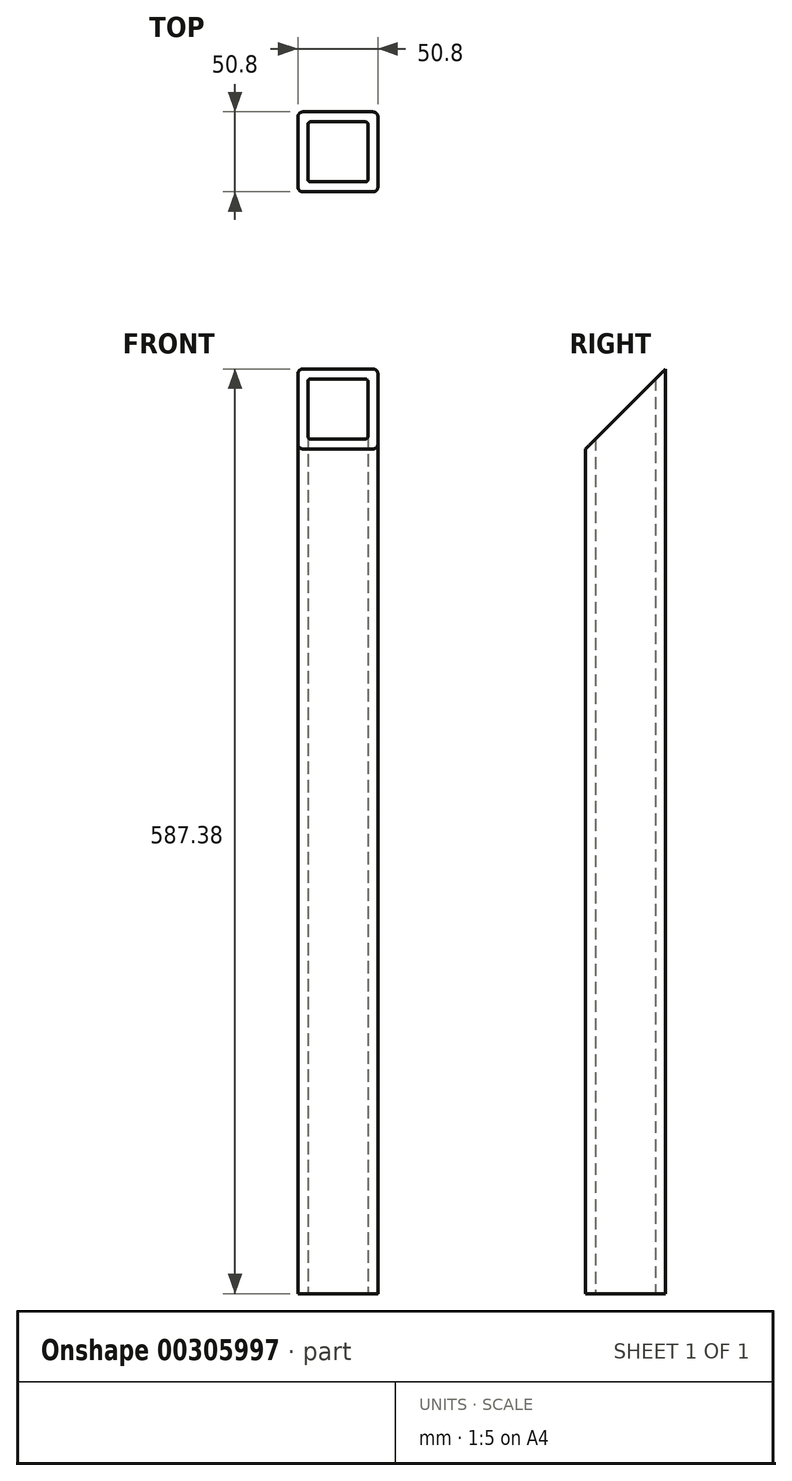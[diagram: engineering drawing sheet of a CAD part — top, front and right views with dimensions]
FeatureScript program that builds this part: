
annotation { "Feature Type Name" : "Feature", "Feature Type Description" : "" }
export const myFeature = defineFeature(function(context is Context, id is Id, definition is map)
    precondition{}
    {
        {
            var Q0;
            Q0=qCreatedBy(makeId("Top.planeOp"),FACE);
            var sketch = newSketch(context, id + "F0", { "sketchPlane" : qUnion([Q0])});
            skLineSegment(sketch, "E0.bottom", {"start": v(-22.22, 25.4) * mm, "end": v(22.23, 25.4) * mm});
            skLineSegment(sketch, "E0.top", {"start": v(-22.23, -25.4) * mm, "end": v(22.23, -25.4) * mm});
            skLineSegment(sketch, "E0.left", {"start": v(-25.4, 22.22) * mm, "end": v(-25.4, -22.23) * mm});
            skLineSegment(sketch, "E0.right", {"start": v(25.4, 22.22) * mm, "end": v(25.4, -22.23) * mm});
            skPoint(sketch, "E0.middle", {"position": v(0, 0) * mm});
            skPoint(sketch, "E1.visualSharp", {"position": v(-25.4, 25.4) * mm});
            skArc(sketch, "E1.filletArc", {"start": v(-22.22, 25.4) * mm, "mid": v(-24.47, 24.47) * mm, "end": v(-25.4, 22.22) * mm});
            skPoint(sketch, "E2.visualSharp", {"position": v(-25.4, -25.4) * mm});
            skArc(sketch, "E2.filletArc", {"start": v(-25.4, -22.23) * mm, "mid": v(-24.47, -24.47) * mm, "end": v(-22.23, -25.4) * mm});
            skPoint(sketch, "E3.visualSharp", {"position": v(25.4, -25.4) * mm});
            skArc(sketch, "E3.filletArc", {"start": v(22.23, -25.4) * mm, "mid": v(24.47, -24.47) * mm, "end": v(25.4, -22.23) * mm});
            skPoint(sketch, "E4.visualSharp", {"position": v(25.4, 25.4) * mm});
            skArc(sketch, "E4.filletArc", {"start": v(25.4, 22.22) * mm, "mid": v(24.47, 24.47) * mm, "end": v(22.23, 25.4) * mm});
            skLineSegment(sketch, "E5.0", {"start": v(-17.46, 19.05) * mm, "end": v(17.46, 19.05) * mm});
            skLineSegment(sketch, "E5.1", {"start": v(-19.05, 17.46) * mm, "end": v(-19.05, -17.46) * mm});
            skLineSegment(sketch, "E5.2", {"start": v(-17.46, -19.05) * mm, "end": v(17.46, -19.05) * mm});
            skLineSegment(sketch, "E5.3", {"start": v(19.05, 17.46) * mm, "end": v(19.05, -17.46) * mm});
            skPoint(sketch, "E6.visualSharp", {"position": v(-19.05, 19.05) * mm});
            skArc(sketch, "E6.filletArc", {"start": v(-17.46, 19.05) * mm, "mid": v(-18.59, 18.59) * mm, "end": v(-19.05, 17.46) * mm});
            skPoint(sketch, "E7.visualSharp", {"position": v(-19.05, -19.05) * mm});
            skArc(sketch, "E7.filletArc", {"start": v(-19.05, -17.46) * mm, "mid": v(-18.59, -18.59) * mm, "end": v(-17.46, -19.05) * mm});
            skPoint(sketch, "E8.visualSharp", {"position": v(19.05, -19.05) * mm});
            skArc(sketch, "E8.filletArc", {"start": v(17.46, -19.05) * mm, "mid": v(18.59, -18.59) * mm, "end": v(19.05, -17.46) * mm});
            skPoint(sketch, "E9.visualSharp", {"position": v(19.05, 19.05) * mm});
            skArc(sketch, "E9.filletArc", {"start": v(19.05, 17.46) * mm, "mid": v(18.59, 18.59) * mm, "end": v(17.46, 19.05) * mm});
            skSolve(sketch);
        }
        {
            var Q0;
            Q0=makeQuery(id+"F0.imprint","IMPRINT",FACE,{"disambiguationData":[TD([[makeQuery(id+"F0.imprint","IMPRINT",EDGE,{"derivedFrom":sQuery(id+"F0.wireOp",EDGE,"E0.bottom")}),-1.0]])]});
            extrude(context, id + "F1", {"entities" : qUnion([Q0]), "depth" : 587.38 * mm});
        }
        {
            var Q0;
            Q0=makeQuery(id+"F1.opExtrude","SWEPT_FACE",FACE,{"disambiguationData":[OSD([sQuery(id+"F0.wireOp",EDGE,"E0.right")])]});
            var sketch = newSketch(context, id + "F2", { "sketchPlane" : qUnion([Q0])});
            skLineSegment(sketch, "E10", {"start": v(25.4, 587.38) * mm, "end": v(-25.4, 536.58) * mm});
            skLineSegment(sketch, "E11", {"start": v(-25.4, 536.58) * mm, "end": v(-25.4, 587.38) * mm});
            skLineSegment(sketch, "E12", {"start": v(-25.4, 587.38) * mm, "end": v(25.4, 587.38) * mm});
            skSolve(sketch);
        }
        {
            var Q0;
            Q0 = qSketchRegion(id + "F2", true);
            extrude(context, id + "F3", {"entities" : qUnion([Q0]), "operationType" : NewBodyOperationType.REMOVE, "endBound" : BoundingType.THROUGH_ALL, "oppositeDirection" : true, "depth" : 25.4 * mm});
        }
    });
